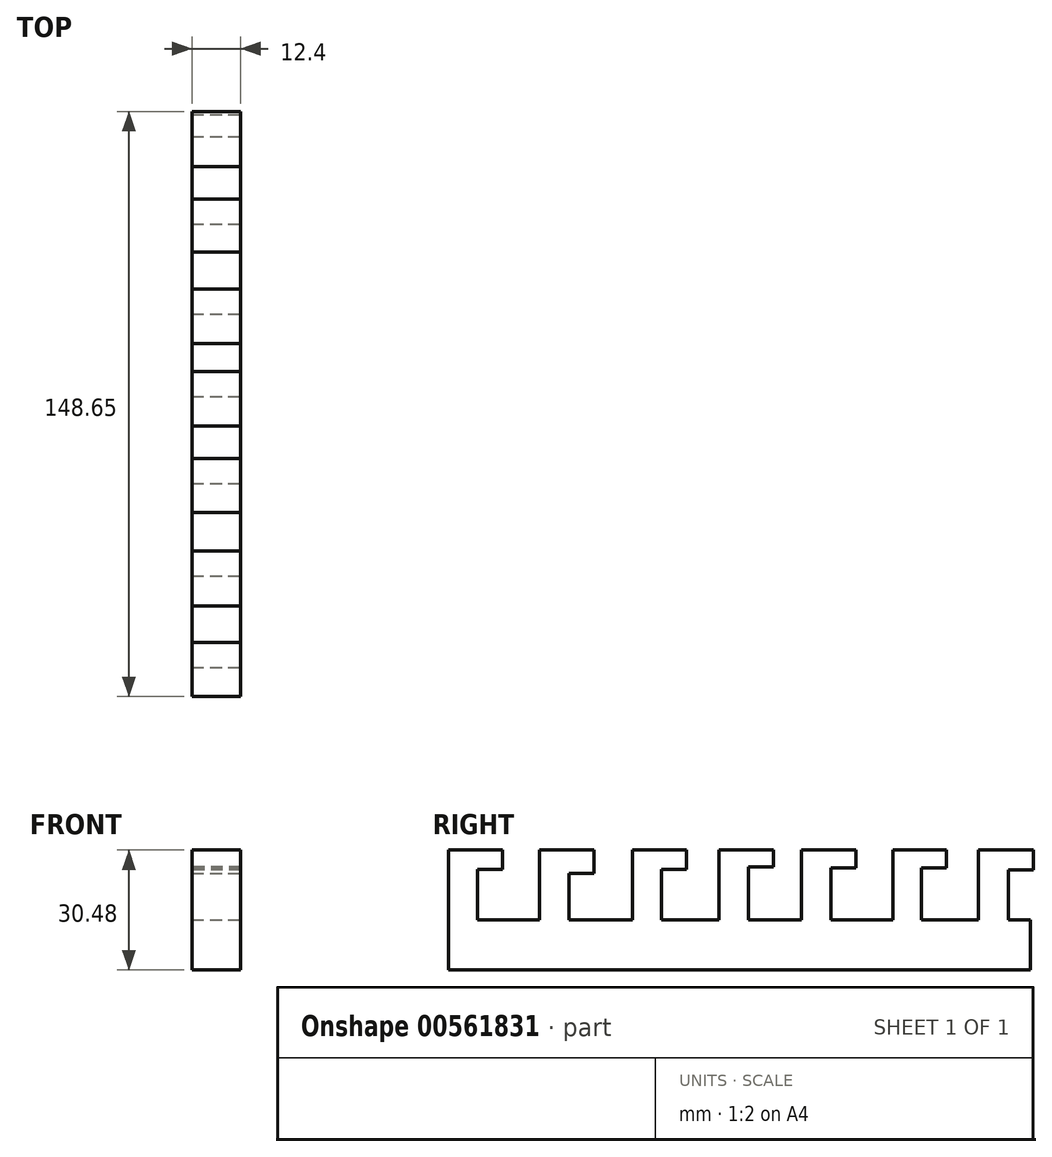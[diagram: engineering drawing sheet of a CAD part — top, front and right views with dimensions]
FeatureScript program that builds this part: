
annotation { "Feature Type Name" : "Feature", "Feature Type Description" : "" }
export const myFeature = defineFeature(function(context is Context, id is Id, definition is map)
    precondition{}
    {
        {
            var Q0;
            Q0=qCreatedBy(makeId("Top.planeOp"),FACE);
            var sketch = newSketch(context, id + "F0", { "sketchPlane" : qUnion([Q0])});
            skLineSegment(sketch, "E0.bottom", {"start": v(-42.26, -73.9) * mm, "end": v(-29.86, -73.9) * mm});
            skLineSegment(sketch, "E0.top", {"start": v(-42.26, 73.96) * mm, "end": v(-29.86, 73.96) * mm});
            skLineSegment(sketch, "E0.left", {"start": v(-42.26, -73.9) * mm, "end": v(-42.26, 73.96) * mm});
            skLineSegment(sketch, "E0.right", {"start": v(-29.86, -73.9) * mm, "end": v(-29.86, 73.96) * mm});
            skSolve(sketch);
        }
        {
            var Q0;
            Q0=makeQuery(id+"F0.imprint","IMPRINT",FACE,{"disambiguationData":[TD([[makeQuery(id+"F0.imprint","IMPRINT",EDGE,{"derivedFrom":sQuery(id+"F0.wireOp",EDGE,"E0.bottom")}),1.0]])]});
            extrude(context, id + "F1", {"entities" : qUnion([Q0]), "depth" : 12.7 * mm, "offsetDistance" : 25.4 * mm});
        }
        {
            var Q0;
            Q0=makeQuery(id+"F1.opExtrude","CAP_FACE",FACE,{"disambiguationData":[OSD([sQuery(id+"F0.wireOp",EDGE,"E0.bottom"),sQuery(id+"F0.wireOp",EDGE,"E0.top"),sQuery(id+"F0.wireOp",EDGE,"E0.left"),sQuery(id+"F0.wireOp",EDGE,"E0.right")])],"isStart":false});
            var sketch = newSketch(context, id + "F2", { "sketchPlane" : qUnion([Q0])});
            skLineSegment(sketch, "E1.bottom", {"start": v(-42.26, -73.9) * mm, "end": v(-29.86, -73.9) * mm});
            skLineSegment(sketch, "E1.top", {"start": v(-42.26, -66.53) * mm, "end": v(-29.86, -66.53) * mm});
            skLineSegment(sketch, "E1.left", {"start": v(-42.26, -73.9) * mm, "end": v(-42.26, -66.53) * mm});
            skLineSegment(sketch, "E1.right", {"start": v(-29.86, -73.9) * mm, "end": v(-29.86, -66.53) * mm});
            skLineSegment(sketch, "E2.bottom", {"start": v(-42.26, -50.82) * mm, "end": v(-29.86, -50.82) * mm});
            skLineSegment(sketch, "E2.top", {"start": v(-42.26, -43.24) * mm, "end": v(-29.86, -43.24) * mm});
            skLineSegment(sketch, "E2.left", {"start": v(-42.26, -50.82) * mm, "end": v(-42.26, -43.24) * mm});
            skLineSegment(sketch, "E2.right", {"start": v(-29.86, -50.82) * mm, "end": v(-29.86, -43.24) * mm});
            skLineSegment(sketch, "E3.bottom", {"start": v(-42.26, -27.07) * mm, "end": v(-29.86, -27.07) * mm});
            skLineSegment(sketch, "E3.top", {"start": v(-42.26, -19.7) * mm, "end": v(-29.86, -19.7) * mm});
            skLineSegment(sketch, "E3.left", {"start": v(-42.26, -27.07) * mm, "end": v(-42.26, -19.7) * mm});
            skLineSegment(sketch, "E3.right", {"start": v(-29.86, -27.07) * mm, "end": v(-29.86, -19.7) * mm});
            skLineSegment(sketch, "E4.bottom", {"start": v(-42.26, -5.18) * mm, "end": v(-29.86, -5.18) * mm});
            skLineSegment(sketch, "E4.top", {"start": v(-42.26, 2.3) * mm, "end": v(-29.86, 2.3) * mm});
            skLineSegment(sketch, "E4.left", {"start": v(-42.26, -5.18) * mm, "end": v(-42.26, 2.3) * mm});
            skLineSegment(sketch, "E4.right", {"start": v(-29.86, -5.18) * mm, "end": v(-29.86, 2.3) * mm});
            skLineSegment(sketch, "E5.bottom", {"start": v(-42.26, 15.8) * mm, "end": v(-29.86, 15.8) * mm});
            skLineSegment(sketch, "E5.top", {"start": v(-42.26, 23.27) * mm, "end": v(-29.86, 23.27) * mm});
            skLineSegment(sketch, "E5.left", {"start": v(-42.26, 15.8) * mm, "end": v(-42.26, 23.27) * mm});
            skLineSegment(sketch, "E5.right", {"start": v(-29.86, 15.8) * mm, "end": v(-29.86, 23.27) * mm});
            skLineSegment(sketch, "E6.bottom", {"start": v(-42.26, 39) * mm, "end": v(-29.86, 39) * mm});
            skLineSegment(sketch, "E6.top", {"start": v(-42.26, 46.21) * mm, "end": v(-29.86, 46.21) * mm});
            skLineSegment(sketch, "E6.left", {"start": v(-42.26, 39) * mm, "end": v(-42.26, 46.21) * mm});
            skLineSegment(sketch, "E6.right", {"start": v(-29.86, 39) * mm, "end": v(-29.86, 46.21) * mm});
            skLineSegment(sketch, "E7.bottom", {"start": v(-42.26, 60.78) * mm, "end": v(-29.86, 60.78) * mm});
            skLineSegment(sketch, "E7.top", {"start": v(-42.26, 68.4) * mm, "end": v(-29.86, 68.4) * mm});
            skLineSegment(sketch, "E7.left", {"start": v(-42.26, 60.78) * mm, "end": v(-42.26, 68.4) * mm});
            skLineSegment(sketch, "E7.right", {"start": v(-29.86, 60.78) * mm, "end": v(-29.86, 68.4) * mm});
            skSolve(sketch);
        }
        {
            var Q0;
            Q0=makeQuery(id+"F2.imprint","IMPRINT",FACE,{"disambiguationData":[TD([[makeQuery(id+"F2.imprint","IMPRINT",EDGE,{"derivedFrom":sQuery(id+"F2.wireOp",EDGE,"E2.bottom")}),1.0]])]});
            var Q1;
            Q1=makeQuery(id+"F2.imprint","IMPRINT",FACE,{"disambiguationData":[TD([[makeQuery(id+"F2.imprint","IMPRINT",EDGE,{"derivedFrom":sQuery(id+"F2.wireOp",EDGE,"E3.bottom")}),1.0]])]});
            var Q2;
            Q2=makeQuery(id+"F2.imprint","IMPRINT",FACE,{"disambiguationData":[TD([[makeQuery(id+"F2.imprint","IMPRINT",EDGE,{"derivedFrom":sQuery(id+"F2.wireOp",EDGE,"E4.bottom")}),1.0]])]});
            var Q3;
            Q3=makeQuery(id+"F2.imprint","IMPRINT",FACE,{"disambiguationData":[TD([[makeQuery(id+"F2.imprint","IMPRINT",EDGE,{"derivedFrom":sQuery(id+"F2.wireOp",EDGE,"E5.bottom")}),1.0]])]});
            var Q4;
            Q4=makeQuery(id+"F2.imprint","IMPRINT",FACE,{"disambiguationData":[TD([[makeQuery(id+"F2.imprint","IMPRINT",EDGE,{"derivedFrom":sQuery(id+"F2.wireOp",EDGE,"E6.bottom")}),1.0]])]});
            var Q5;
            Q5=makeQuery(id+"F2.imprint","IMPRINT",FACE,{"disambiguationData":[TD([[makeQuery(id+"F2.imprint","IMPRINT",EDGE,{"derivedFrom":sQuery(id+"F2.wireOp",EDGE,"E7.bottom")}),1.0]])]});
            var Q6;
            Q6=makeQuery(id+"F2.imprint","IMPRINT",FACE,{"disambiguationData":[TD([[makeQuery(id+"F2.imprint","IMPRINT",EDGE,{"derivedFrom":sQuery(id+"F2.wireOp",EDGE,"E1.bottom")}),1.0]])]});
            extrude(context, id + "F3", {"entities" : qUnion([Q0, Q1, Q2, Q3, Q4, Q5, Q6]), "operationType" : NewBodyOperationType.ADD, "depth" : 17.78 * mm, "offsetDistance" : 25.4 * mm});
        }
        {
            var Q0;
            Q0=makeQuery(id+"F3.opExtrude","SWEPT_FACE",FACE,{"disambiguationData":[OSD([sQuery(id+"F2.wireOp",EDGE,"E1.top")])]});
            var sketch = newSketch(context, id + "F4", { "sketchPlane" : qUnion([Q0])});
            skLineSegment(sketch, "E8.bottom", {"start": v(29.86, 30.48) * mm, "end": v(42.26, 30.48) * mm});
            skLineSegment(sketch, "E8.top", {"start": v(29.86, 25.54) * mm, "end": v(42.26, 25.54) * mm});
            skLineSegment(sketch, "E8.left", {"start": v(29.86, 30.48) * mm, "end": v(29.86, 25.54) * mm});
            skLineSegment(sketch, "E8.right", {"start": v(42.26, 30.48) * mm, "end": v(42.26, 25.54) * mm});
            skSolve(sketch);
        }
        {
            var Q0;
            Q0=makeQuery(id+"F4.imprint","IMPRINT",FACE,{"disambiguationData":[TD([[makeQuery(id+"F4.imprint","IMPRINT",EDGE,{"derivedFrom":sQuery(id+"F4.wireOp",EDGE,"E8.bottom")}),1.0]])]});
            extrude(context, id + "F5", {"entities" : qUnion([Q0]), "operationType" : NewBodyOperationType.ADD, "depth" : 6.35 * mm, "offsetDistance" : 25.4 * mm});
        }
        {
            var Q0;
            Q0=makeQuery(id+"F3.opExtrude","SWEPT_FACE",FACE,{"disambiguationData":[OSD([sQuery(id+"F2.wireOp",EDGE,"E2.top")])]});
            var sketch = newSketch(context, id + "F6", { "sketchPlane" : qUnion([Q0])});
            skLineSegment(sketch, "E9.bottom", {"start": v(42.26, 30.48) * mm, "end": v(29.86, 30.48) * mm});
            skLineSegment(sketch, "E9.top", {"start": v(42.26, 24.6) * mm, "end": v(29.86, 24.6) * mm});
            skLineSegment(sketch, "E9.left", {"start": v(42.26, 30.48) * mm, "end": v(42.26, 24.6) * mm});
            skLineSegment(sketch, "E9.right", {"start": v(29.86, 30.48) * mm, "end": v(29.86, 24.6) * mm});
            skSolve(sketch);
        }
        {
            var Q0;
            Q0=makeQuery(id+"F3.opExtrude","SWEPT_FACE",FACE,{"disambiguationData":[OSD([sQuery(id+"F2.wireOp",EDGE,"E3.top")])]});
            var sketch = newSketch(context, id + "F7", { "sketchPlane" : qUnion([Q0])});
            skLineSegment(sketch, "E10.bottom", {"start": v(29.86, 30.48) * mm, "end": v(42.26, 30.48) * mm});
            skLineSegment(sketch, "E10.top", {"start": v(29.86, 25.51) * mm, "end": v(42.26, 25.51) * mm});
            skLineSegment(sketch, "E10.left", {"start": v(29.86, 30.48) * mm, "end": v(29.86, 25.51) * mm});
            skLineSegment(sketch, "E10.right", {"start": v(42.26, 30.48) * mm, "end": v(42.26, 25.51) * mm});
            skSolve(sketch);
        }
        {
            var Q0;
            Q0=makeQuery(id+"F3.opExtrude","SWEPT_FACE",FACE,{"disambiguationData":[OSD([sQuery(id+"F2.wireOp",EDGE,"E4.top")])]});
            var sketch = newSketch(context, id + "F8", { "sketchPlane" : qUnion([Q0])});
            skLineSegment(sketch, "E11.bottom", {"start": v(29.86, 30.48) * mm, "end": v(42.26, 30.48) * mm});
            skLineSegment(sketch, "E11.top", {"start": v(29.86, 26.23) * mm, "end": v(42.26, 26.23) * mm});
            skLineSegment(sketch, "E11.left", {"start": v(29.86, 30.48) * mm, "end": v(29.86, 26.23) * mm});
            skLineSegment(sketch, "E11.right", {"start": v(42.26, 30.48) * mm, "end": v(42.26, 26.23) * mm});
            skSolve(sketch);
        }
        {
            var Q0;
            Q0=makeQuery(id+"F3.opExtrude","SWEPT_FACE",FACE,{"disambiguationData":[OSD([sQuery(id+"F2.wireOp",EDGE,"E5.top")])]});
            var sketch = newSketch(context, id + "F9", { "sketchPlane" : qUnion([Q0])});
            skLineSegment(sketch, "E12.bottom", {"start": v(29.86, 30.48) * mm, "end": v(42.26, 30.48) * mm});
            skLineSegment(sketch, "E12.top", {"start": v(29.86, 25.98) * mm, "end": v(42.26, 25.98) * mm});
            skLineSegment(sketch, "E12.left", {"start": v(29.86, 30.48) * mm, "end": v(29.86, 25.98) * mm});
            skLineSegment(sketch, "E12.right", {"start": v(42.26, 30.48) * mm, "end": v(42.26, 25.98) * mm});
            skSolve(sketch);
        }
        {
            var Q0;
            Q0=makeQuery(id+"F3.opExtrude","SWEPT_FACE",FACE,{"disambiguationData":[OSD([sQuery(id+"F2.wireOp",EDGE,"E6.top")])]});
            var sketch = newSketch(context, id + "F10", { "sketchPlane" : qUnion([Q0])});
            skLineSegment(sketch, "E13.bottom", {"start": v(29.86, 30.48) * mm, "end": v(42.26, 30.48) * mm});
            skLineSegment(sketch, "E13.top", {"start": v(29.86, 25.94) * mm, "end": v(42.26, 25.94) * mm});
            skLineSegment(sketch, "E13.left", {"start": v(29.86, 30.48) * mm, "end": v(29.86, 25.94) * mm});
            skLineSegment(sketch, "E13.right", {"start": v(42.26, 30.48) * mm, "end": v(42.26, 25.94) * mm});
            skSolve(sketch);
        }
        {
            var Q0;
            Q0=makeQuery(id+"F3.opExtrude","SWEPT_FACE",FACE,{"disambiguationData":[OSD([sQuery(id+"F2.wireOp",EDGE,"E7.top")])]});
            var sketch = newSketch(context, id + "F11", { "sketchPlane" : qUnion([Q0])});
            skLineSegment(sketch, "E14.bottom", {"start": v(29.86, 30.48) * mm, "end": v(42.26, 30.48) * mm});
            skLineSegment(sketch, "E14.top", {"start": v(29.86, 25.43) * mm, "end": v(42.26, 25.43) * mm});
            skLineSegment(sketch, "E14.left", {"start": v(29.86, 30.48) * mm, "end": v(29.86, 25.43) * mm});
            skLineSegment(sketch, "E14.right", {"start": v(42.26, 30.48) * mm, "end": v(42.26, 25.43) * mm});
            skSolve(sketch);
        }
        {
            var Q0;
            Q0=makeQuery(id+"F6.imprint","IMPRINT",FACE,{"disambiguationData":[TD([[makeQuery(id+"F6.imprint","IMPRINT",EDGE,{"derivedFrom":sQuery(id+"F6.wireOp",EDGE,"E9.bottom")}),1.0]])]});
            var Q1;
            Q1=makeQuery(id+"F8.imprint","IMPRINT",FACE,{"disambiguationData":[TD([[makeQuery(id+"F8.imprint","IMPRINT",EDGE,{"derivedFrom":sQuery(id+"F8.wireOp",EDGE,"E11.bottom")}),1.0]])]});
            var Q2;
            Q2=makeQuery(id+"F9.imprint","IMPRINT",FACE,{"disambiguationData":[TD([[makeQuery(id+"F9.imprint","IMPRINT",EDGE,{"derivedFrom":sQuery(id+"F9.wireOp",EDGE,"E12.bottom")}),1.0]])]});
            var Q3;
            Q3=makeQuery(id+"F10.imprint","IMPRINT",FACE,{"disambiguationData":[TD([[makeQuery(id+"F10.imprint","IMPRINT",EDGE,{"derivedFrom":sQuery(id+"F10.wireOp",EDGE,"E13.bottom")}),1.0]])]});
            var Q4;
            Q4=makeQuery(id+"F11.imprint","IMPRINT",FACE,{"disambiguationData":[TD([[makeQuery(id+"F11.imprint","IMPRINT",EDGE,{"derivedFrom":sQuery(id+"F11.wireOp",EDGE,"E14.bottom")}),1.0]])]});
            extrude(context, id + "F12", {"entities" : qUnion([Q0, Q1, Q2, Q3, Q4]), "operationType" : NewBodyOperationType.ADD, "depth" : 6.35 * mm, "offsetDistance" : 25.4 * mm});
        }
        {
            var Q0;
            Q0=makeQuery(id+"F7.imprint","IMPRINT",FACE,{"disambiguationData":[TD([[makeQuery(id+"F7.imprint","IMPRINT",EDGE,{"derivedFrom":sQuery(id+"F7.wireOp",EDGE,"E10.bottom")}),1.0]])]});
            extrude(context, id + "F13", {"entities" : qUnion([Q0]), "operationType" : NewBodyOperationType.ADD, "depth" : 6.35 * mm, "offsetDistance" : 25.4 * mm});
        }
    });
